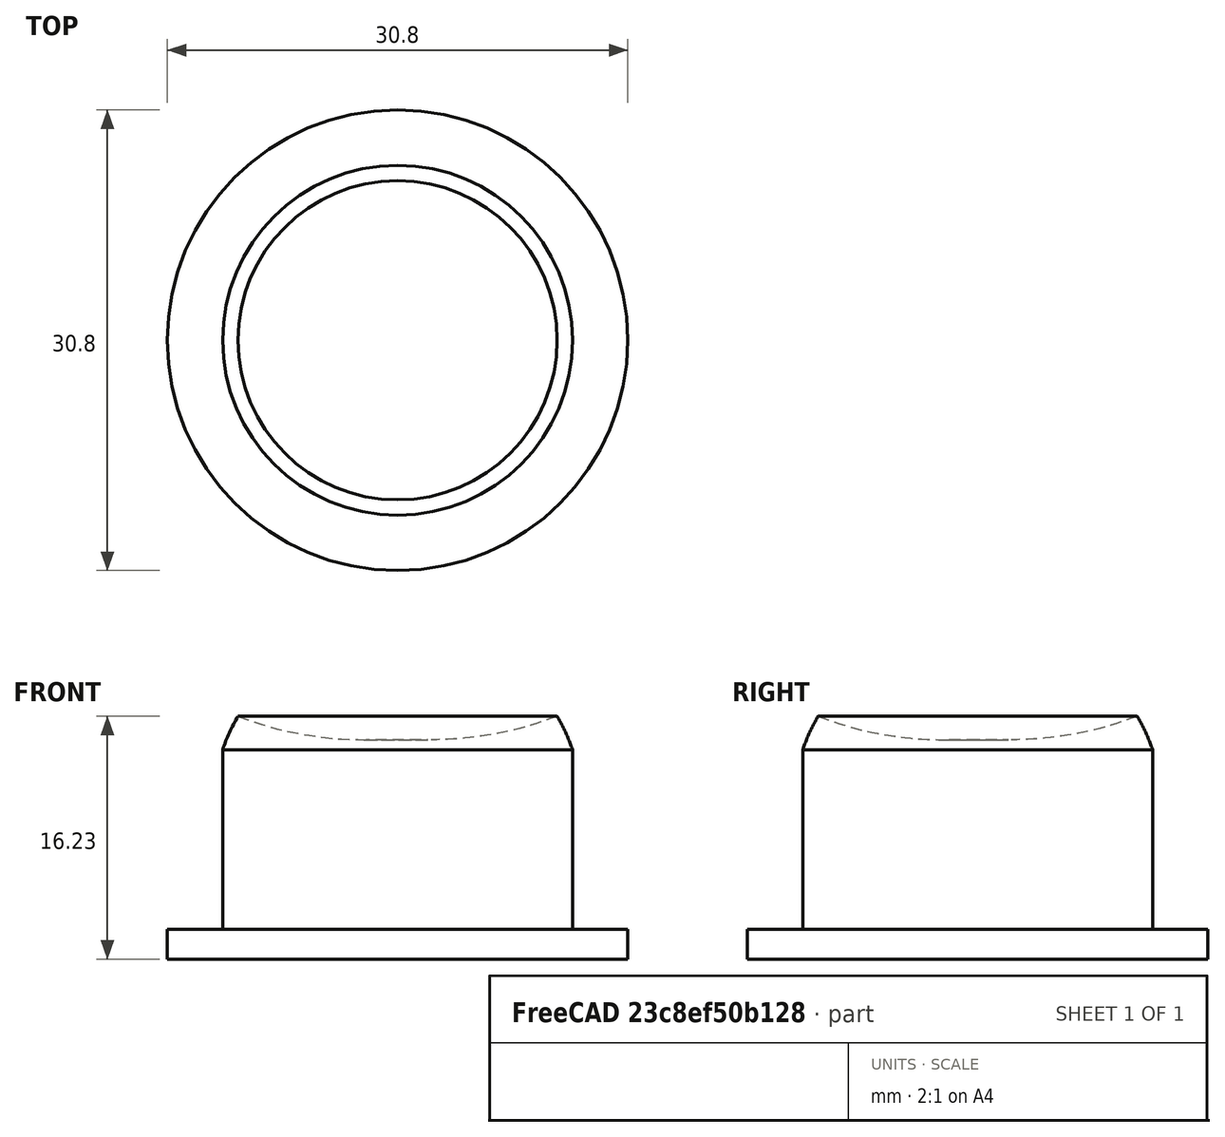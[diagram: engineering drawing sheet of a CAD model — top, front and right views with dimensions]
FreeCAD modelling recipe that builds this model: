
FCSTD DOCUMENT  (FreeCAD 0.20R29177 +426 (Git))
Label: button_presser
License: All rights reserved
LicenseURL: http://en.wikipedia.org/wiki/All_rights_reserved
objects: Sketcher::SketchObject×1, Spreadsheet::Sheet×1, PartDesign::Revolution×1, PartDesign::Body×1
note: 4 computed .brp shape members not serialized (recipe doc carries the construction recipe); baked Part::Feature solids carry a one-line shape summary decoded from their .brp
EXTERNAL_REF file=button_base_holder.FCStd obj=Sketch006
EXTERNAL_REF file=button_case.FCStd obj=Spreadsheet

FEATURE [Sketcher::SketchObject] Sketch
  FullyConstrained = false
  MapMode = 5
  Placement = pos=(0,0,0) rot=(1,0,0;1.5708rad)
  Support = -> [XZ_Plane]
  expr: Constraints[11] = <<button_base_holder>>#<<Sketch006>>.Constraints.inner_rad - <<press_data>>.space * 0.5
  expr: Constraints[12] = <<button_base_holder>>#<<Sketch006>>.Constraints.mid_dia / 2 - <<press_data>>.space
  expr: Constraints[13] = <<press_data>>.bot_thick
  expr: Constraints[23] = <<button_case>>#<<button_data>>.button_big_thick + <<button_case>>#<<button_data>>.button_thick
  sketch-geometry (10):
    g0: LineSegment StartX=0 StartY=0 StartZ=0 EndX=-15.4 EndY=0 EndZ=0
    g1: LineSegment StartX=-15.4 StartY=0 StartZ=0 EndX=-15.4 EndY=2 EndZ=0
    g2: LineSegment StartX=-15.4 StartY=2 StartZ=0 EndX=-11.7 EndY=2 EndZ=0
    g3: LineSegment StartX=-11.7 StartY=2 StartZ=0 EndX=-11.7 EndY=14 EndZ=0
    g4: ArcOfCircle CenterX=-0.0575136 CenterY=9.99606 CenterZ=0 NormalX=0 NormalY=0 NormalZ=1 AngleXU=0 Radius=12.3117 StartAngle=2.61028 EndAngle=2.81036
    g5: LineSegment StartX=-11.7 StartY=14 StartZ=0 EndX=0 EndY=14 EndZ=0
    g6: ArcOfCircle CenterX=-2.24838 CenterY=38.1135 CenterZ=0 NormalX=0 NormalY=0 NormalZ=1 AngleXU=0 Radius=23.445 StartAngle=4.34488 EndAngle=4.71873
    g7: LineSegment StartX=-2.09977 StartY=14.6689 StartZ=0 EndX=0 EndY=14.6689 EndZ=0
    g8: LineSegment StartX=0 StartY=14.6689 StartZ=0 EndX=0 EndY=14 EndZ=0
    g9: LineSegment StartX=0 StartY=14 StartZ=0 EndX=0 EndY=0 EndZ=0
  constraints (24):
    c: Coincident(g-1,g0)
    c: PointOnObject(g0,g-1)
    c: Coincident(g0,g1)
    c: Vertical(g1)
    c: Coincident(g1,g2)
    c: Horizontal(g2)
    c: Coincident(g2,g3)
    c: Vertical(g3)
    c: Coincident(g4,g3)
    c: Coincident(g5,g3)
    c: Horizontal(g5)
    c: DistanceX(g2,g0) = 11.7
    c: DistanceX(g0,g0) = 15.4
    c: DistanceY(g1,g1) = 2
    c: Coincident(g6,g4)
    c: Coincident(g7,g6)
    c: Horizontal(g7)
    c: PointOnObject(g7,g-2)
    c: Coincident(g8,g7)
    c: Coincident(g8,g5)
    c: Coincident(g9,g8)
    c: Coincident(g9,g0)
    c: Vertical(g9)
    c: DistanceY(g3,g3) = 12
FEATURE [Spreadsheet::Sheet] Spreadsheet  label="press_data"
  cells = A2=space; B2(space)==0.6mm; A3=bot_thick; B3(bot_thick)==2mm
FEATURE [PartDesign::Revolution] Revolution
  Angle = 360
  Axis = (0,2e-16,1)
  Base = (0,0,0)
  Placement = pos=(0,0,0) rot=(1,0,0;1.5708rad)
  Profile = -> Sketch
  ReferenceAxis = -> Sketch [V_Axis]
FEATURE [PartDesign::Body] Body
  Group = -> [Sketch,Revolution]
  Origin = -> Origin
  Tip = -> Revolution
